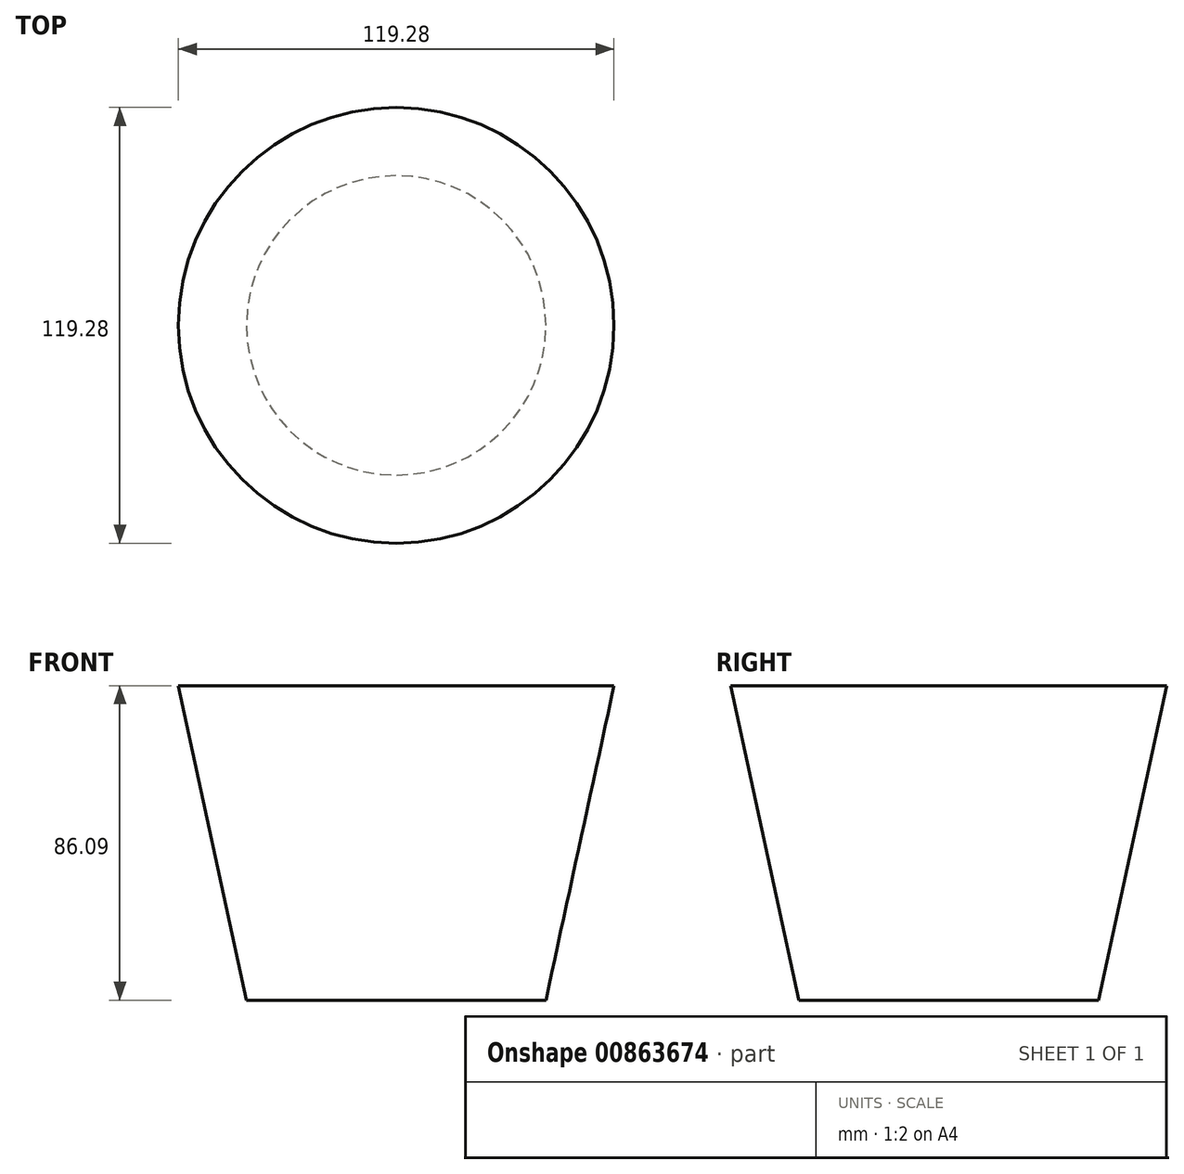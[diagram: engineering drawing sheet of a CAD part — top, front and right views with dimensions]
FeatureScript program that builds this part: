
annotation { "Feature Type Name" : "Feature", "Feature Type Description" : "" }
export const myFeature = defineFeature(function(context is Context, id is Id, definition is map)
    precondition{}
    {
        {
            var Q0;
            Q0=qCreatedBy(makeId("Front.planeOp"),FACE);
            var sketch = newSketch(context, id + "F0", { "sketchPlane" : qUnion([Q0])});
            skLineSegment(sketch, "E0", {"start": v(0, 0) * mm, "end": v(40.98, 0) * mm});
            skLineSegment(sketch, "E1", {"start": v(40.98, 0) * mm, "end": v(59.64, 86.1) * mm});
            skLineSegment(sketch, "E2", {"start": v(59.64, 86.1) * mm, "end": v(0, 86.1) * mm});
            skLineSegment(sketch, "E3", {"start": v(0, 86.1) * mm, "end": v(0, 0) * mm});
            skSolve(sketch);
        }
        {
            var Q0;
            Q0 = qSketchRegion(id + "F0", true);
            var Q1;
            Q1=sQuery(id+"F0.wireOp",EDGE,"E3");
            revolve(context, id + "F1", {"surfaceOperationType" : NewSurfaceOperationType.NEW, "entities" : qUnion([Q0]), "axis" : qUnion([Q1]), "revolveType" : RevolveType.FULL});
        }
    });
